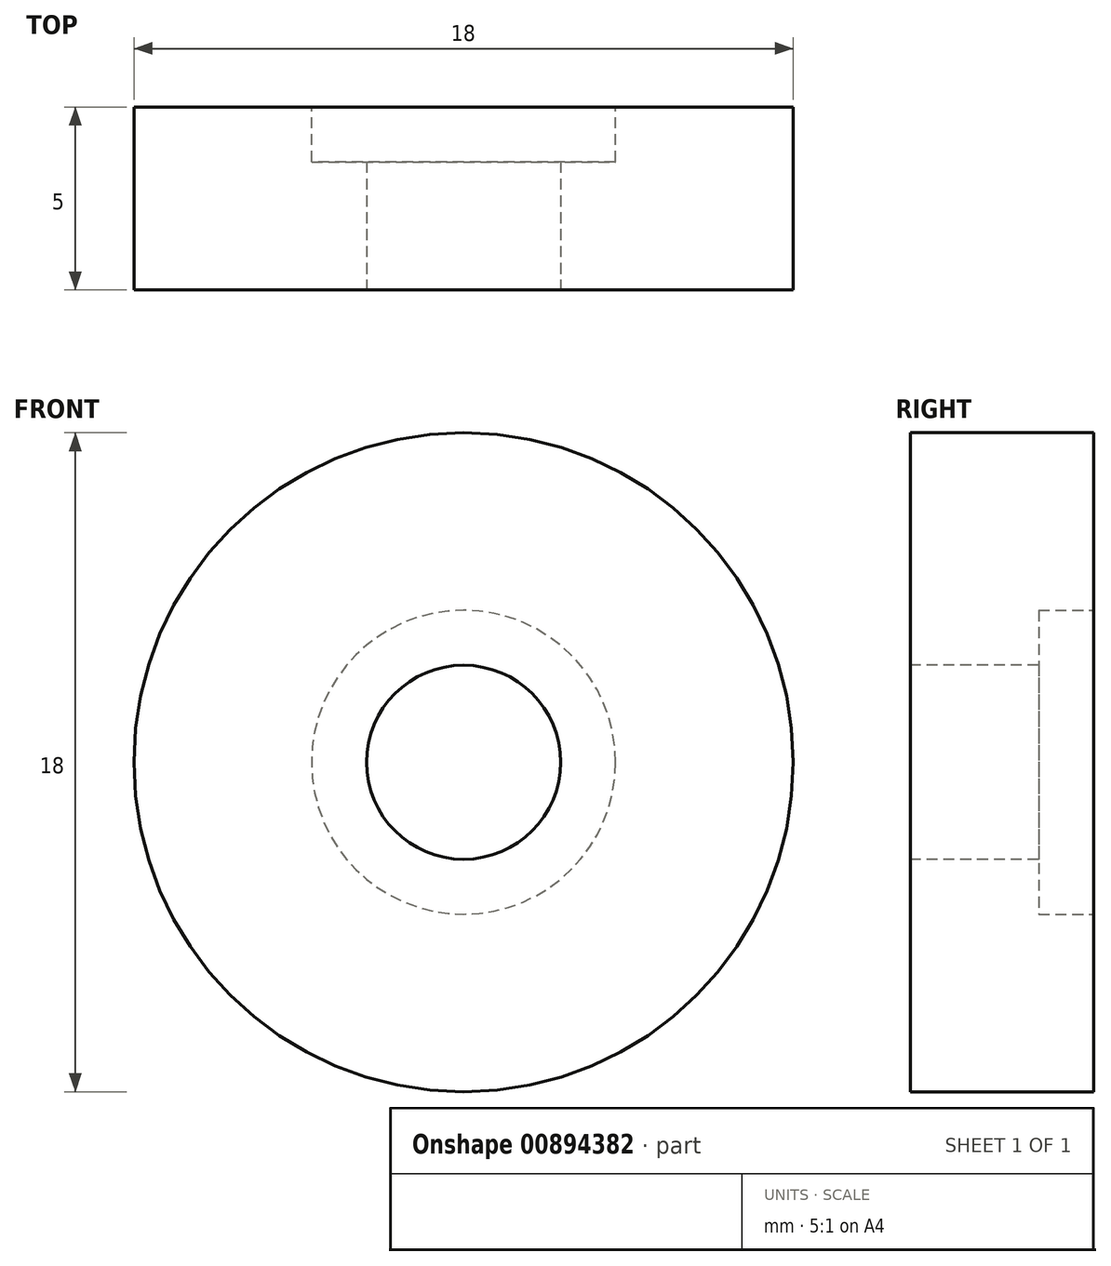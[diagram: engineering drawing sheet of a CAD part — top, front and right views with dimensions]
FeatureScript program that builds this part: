
annotation { "Feature Type Name" : "Feature", "Feature Type Description" : "" }
export const myFeature = defineFeature(function(context is Context, id is Id, definition is map)
    precondition{}
    {
        {
            var Q0;
            Q0=qCreatedBy(makeId("Front.planeOp"),FACE);
            var sketch = newSketch(context, id + "F0", { "sketchPlane" : qUnion([Q0])});
            skCircle(sketch, "E0", {"center": v(0, 0) * mm, "radius": 9 * mm});
            skSolve(sketch);
        }
        {
            var Q0;
            Q0 = qSketchRegion(id + "F0", true);
            extrude(context, id + "F1", {"entities" : qUnion([Q0]), "depth" : 5 * mm, "offsetDistance" : 25 * mm});
        }
        {
            var Q0;
            Q0=makeQuery(id+"F1.opExtrude","CAP_FACE",FACE,{"disambiguationData":[OSD([sQuery(id+"F0.wireOp",EDGE,"E0")])],"isStart":true});
            var sketch = newSketch(context, id + "F2", { "sketchPlane" : qUnion([Q0])});
            skCircle(sketch, "E1", {"center": v(0, 0) * mm, "radius": 4.15 * mm});
            skSolve(sketch);
        }
        {
            var Q0;
            Q0 = qSketchRegion(id + "F2", true);
            extrude(context, id + "F3", {"entities" : qUnion([Q0]), "operationType" : NewBodyOperationType.REMOVE, "oppositeDirection" : true, "depth" : 1.5 * mm, "offsetDistance" : 25 * mm});
        }
        {
            var Q0;
            Q0=makeQuery(id+"F1.opExtrude","CAP_FACE",FACE,{"disambiguationData":[OSD([sQuery(id+"F0.wireOp",EDGE,"E0")])],"isStart":false});
            var sketch = newSketch(context, id + "F4", { "sketchPlane" : qUnion([Q0])});
            skCircle(sketch, "E2", {"center": v(0, 0) * mm, "radius": 2.65 * mm});
            skSolve(sketch);
        }
        {
            var Q0;
            Q0 = qSketchRegion(id + "F4", true);
            extrude(context, id + "F5", {"entities" : qUnion([Q0]), "operationType" : NewBodyOperationType.REMOVE, "endBound" : BoundingType.THROUGH_ALL, "oppositeDirection" : true, "depth" : 25 * mm, "offsetDistance" : 25 * mm});
        }
    });
